# Revit family: KS Husky, Typ IV-19, M16, Ø273-355,6
name_source: partatom
category: HLS-Bauteile
revit_build: Autodesk Revit 2018 (Build: 20190510_1515(x64)
units: mm (PartAtom-declared; Revit-internal decimal feet)

## family parameters
Arbeitsebenenbasiert = Ja
Beim Laden mit Abzugskörper schneiden = Nein
Bemaßung runder Anschluss = Durchmesser verwenden
Gemeinsam genutzt = Ja
Immer vertikal = Nein
Raumberechnungspunkt = Nein
Teiletyp = Normal

## types (3) — shared parameters
Anschluss = M16
Baustoffklasse = B2
DF2 = 20 mm  [stored 0.0656168 ft]
DVS = 13 mm
Dichte Kern = 120 kg/m³
Dämmkörper = KA/PU
Fabrikat = MEFA
Firma = MEFA Befestigungs- und Montagesysteme GmbH
HGA = 15 mm  [stored 0.0492126 ft]
Kurztext1 = Kälteschelle Husky IV 19
L = 66 mm  [stored 0.216535 ft]
MB = 50 mm  [stored 0.164042 ft]
MD = 5 mm  [stored 0.0164042 ft]
Material = Stahl
Material Mantel = Kunststoff
Materialname = S235
Mengeneinheit = St
Oberflaeche = galvanisch verzinkt
Rohrschellentyp = Titan HD
Schalenlänge = 66 mm
Typ = IV 19
Vorgabe-Ansicht = 1219 mm
Wasserdampfdiffusionswiderstand = 7000 µ
Wärmeleitfähigkeit = 0.029 W/mK
max. Temperaturbeständigkeit = 105 °C
mittl. Nenndruckfestigkeit Kern = 1,35 N/mm²
stat. Belastung Kern = 0,27 N/mm²
vpe = 1 St
zero-valued in all types: AB

## per-type parameters (varying)
| type | A | Anschlußhöhe | Artikelnummer | B | Breite | D | D0 | DF1 | DS | Dämmstärke | EAN | Gewicht | Gewicht pro Bauteil | H | Kurztext2 | R | RM | Rohraußendurchmesser Stahl | S | max. zul. Last |
| Kälteschelle Husky, Typ IV-19, M16, Ø323,9 | 47 mm | 43 mm | 68432404 | 457 mm | 457 mm | 324 mm | 377 mm | 17 mm | 27 mm | 27 mm | 4250928440952 | 3.07 kg | 3.07 kg | 402 mm | 323,9 mm Iso 27 x 66 mm M16 | 189 mm | 194 mm | 323,9 mm | 440 mm | 5.33 kN |
| Kälteschelle Husky, Typ IV-19, M16, Ø355,6 | 45 mm | 41 mm | 68435604 | 486 mm | 486 mm | 356 mm | 406 mm | 18 mm  [stored 0.0590551 ft] | 25 mm  [stored 0.082021 ft] | 25 mm  [stored 0.082021 ft] | 4250928440969 | 3.26 kg | 3.26 kg | 431 mm | 355,6 mm Iso 25 x 66 mm M16 | 203 mm | 208 mm | 355,6 mm | 469 mm | 5.74 kN |
| Kälteschelle Husky, Typ IV-19, M16, Ø273 | 46 mm | 42 mm | 68427304 | 404 mm | 402 mm | 273 mm | 324 mm | 17 mm | 26 mm | 26 mm | 4250928440945 | 2.68 kg | 2.68 kg | 349 mm | 273 mm Iso 26 x 66 mm M16 | 162 mm  [stored 0.531496 ft] | 167 mm | 273 mm | 387 mm | 4.58 kN |

note: [stored X ft] marks values corroborated as IEEE doubles in the binary element streams (Revit-internal decimal feet)

## geometry (parser evidence)
native form markers: Sweep x6
no freeform markers — native parametric forms only
